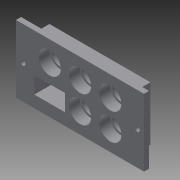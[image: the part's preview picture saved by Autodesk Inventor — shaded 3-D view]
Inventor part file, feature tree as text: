
AUTODESK INVENTOR PART (.ipt)
format: ipt  version: 2014 SP1 (Build 180222100, 222)  size: 162,816 bytes
history: native  units: in
note: dims shown in document units (in); Inventor stores cm internally (conversion verified against a paired STEP export)
features: extrude x5, sketch x5
ambient origin geometry x8: Origin, YZ Plane, XZ Plane, XY Plane, X Axis, Y Axis, Z Axis, Center Point
bodies: Solid1 (feature_tree)
feature tree (10):
  extrude  "Extrusion1"  Depth=1.0in
  extrude  "Extrusion2"  Depth=0.41in
  extrude  "Extrusion3"  Depth=0.41in
  extrude  "Extrusion4"  Depth=0.57in
  extrude  "Extrusion5"  Depth=0.37in TaperAngle=0.0deg
  sketch  "Sketch1"  dims[d0=1.875in d1=1.0in]
  sketch  "Sketch3"  dims[d2=0.41in d3=0.41in]
  sketch  "Sketch4"  dims[d4=0.41in d5=0.41in]
  sketch  "Sketch5"  dims[d6=0.41in d9=0.57in]
  sketch  "Sketch6"  dims[d10=0.31in d13=0.37in d14=0.0in d15=0.276in d16=0.0in d17=0.33in d18=0.17in d19=0.0in d20=45.0deg d21=0.035in d22=0.0in d23=0.094in d24=0.094in d25=0.094in d26=0.0in d27=2.375in d28=1.25in]
